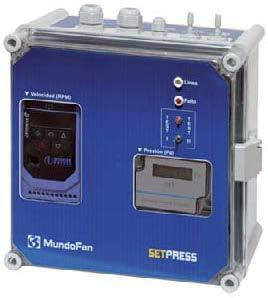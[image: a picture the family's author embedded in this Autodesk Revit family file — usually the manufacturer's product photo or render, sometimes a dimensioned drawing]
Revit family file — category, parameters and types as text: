
# Revit family: SETPRESS-075_VE10809
name_source: partatom
category: Aparatos eléctricos
revit_build: Autodesk Revit 2016 (Build: 20150220_1215(x64)
units: mm (PartAtom-declared; Revit-internal decimal feet)

## family parameters
Compartido = No
Corte con vacíos al cargar = No
Cota de conector redondo = Diámetro de uso
Mantener orientación de anotación = No
Número OmniClass = 23.80.00.00
Punto de cálculo de habitación = No
Se basa en plano de trabajo = No
Siempre vertical = Sí
Tipo de pieza = Caja de conexiones
Título OmniClass = Electric Power and Lighting

## types (1)
- SETPRESS
    Alimentación = 230Vac monofásico
    Corriente = 7 A
    Costo = 0 $
    Código de montaje = VE10809
    Descripción = CONTROL EFICIENCIA ENERGETICA PARA VENTILADORES
    Dimensiones máx. = 270x300x170 mm
    Fabricante = SALVADOR ESCODA
    Imagen de tipo = setpress.jpg
    Leds = linea / fallo
    Modelo = SETPRESS 0,75 kW
    Normativas = UNE-EN 12101-6
    Potencia = 0,75 kW
    Regulación = Mediante sonda analógica de presión
    Salida = 230Vac monofásico
    URL = www.salvadorescoda.com
    Visualización = frecuencia (Hz) y presión (Pa)
